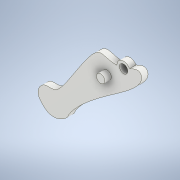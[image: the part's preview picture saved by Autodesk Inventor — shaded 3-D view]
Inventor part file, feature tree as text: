
AUTODESK INVENTOR PART (.ipt)
format: ipt  version: 2022 (Build 260153000, 153)  size: 133,120 bytes
history: native  units: in
note: dims shown in document units (in); Inventor stores cm internally (conversion verified against a paired STEP export)
features: extrude x2, sketch x1
ambient origin geometry x8: Origin, YZ Plane, XZ Plane, XY Plane, X Axis, Y Axis, Z Axis, Center Point
bodies: Solid1 (feature_tree)
feature tree (3):
  sketch  "Sketch2"  dims[d0=0.1969in d1=0.0in d2=0.1969in d3=0.0in d4=0.2559in]
  extrude  "Extrusion1"  Depth=0.1969in TaperAngle=0.0deg
  extrude  "Extrusion2"  Depth=0.2559in
